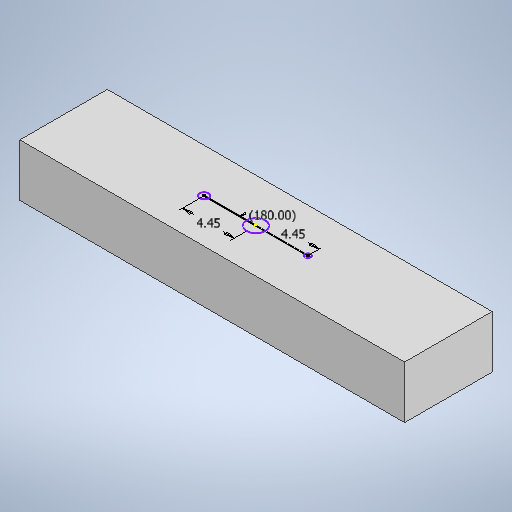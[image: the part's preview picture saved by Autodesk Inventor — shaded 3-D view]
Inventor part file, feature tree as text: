
AUTODESK INVENTOR PART (.ipt)
format: ipt  version: 2025.1 (Build 291241020, 241B)  size: 220,160 bytes
history: native  units: in
note: dims shown in document units (in); Inventor stores cm internally (conversion verified against a paired STEP export)
features: sketch x2, extrude x1
ambient origin geometry x8: Origin, YZ Plane, XZ Plane, XY Plane, X Axis, Y Axis, Z Axis, Center Point
bodies: Solid1 (feature_tree)
feature tree (3):
  extrude  "Extrusion1"  Depth=1.2992in
  sketch  "Sketch2"  dims[d2=0.1772in d3=0.0in d4=0.1752in d5=180.0deg d6=0.1752in]
  sketch  "Sketch1"  dims[d0=0.2953in d1=1.2992in]
